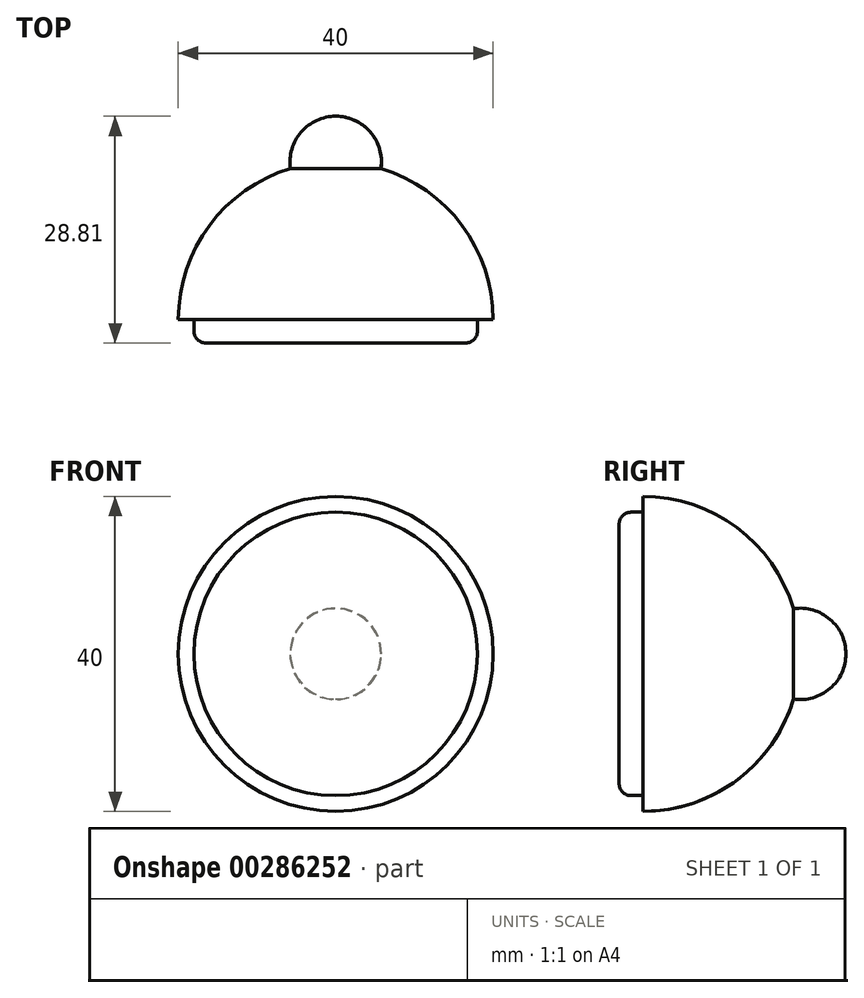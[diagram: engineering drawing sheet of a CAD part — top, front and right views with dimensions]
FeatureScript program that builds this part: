
annotation { "Feature Type Name" : "Feature", "Feature Type Description" : "" }
export const myFeature = defineFeature(function(context is Context, id is Id, definition is map)
    precondition{}
    {
        {
            var Q0;
            Q0=qCreatedBy(makeId("Top.planeOp"),FACE);
            var sketch = newSketch(context, id + "F0", { "sketchPlane" : qUnion([Q0])});
            skPoint(sketch, "E0", {"position": v(0, 20) * mm});
            skPoint(sketch, "E1", {"position": v(20, 0) * mm});
            skArc(sketch, "E2", {"start": v(20, 0) * mm, "mid": v(16.05, 11.94) * mm, "end": v(5.75, 19.16) * mm});
            skLineSegment(sketch, "E3", {"start": v(0, 14.2) * mm, "end": v(0, 0) * mm});
            skLineSegment(sketch, "E4", {"start": v(20, 0) * mm, "end": v(0, 0) * mm});
            skArc(sketch, "E5", {"start": v(5.75, 19.16) * mm, "mid": v(4.4, 23.8) * mm, "end": v(0, 25.8) * mm});
            skLineSegment(sketch, "E6", {"start": v(0, 14.2) * mm, "end": v(0, 25.8) * mm});
            skSolve(sketch);
        }
        {
            var Q0;
            Q0=makeQuery(id+"F0.imprint","IMPRINT",FACE,{"disambiguationData":[TD([[makeQuery(id+"F0.imprint","IMPRINT",EDGE,{"derivedFrom":sQuery(id+"F0.wireOp",EDGE,"E2")}),1.0]])]});
            var Q1;
            Q1=sQuery(id+"F0.wireOp",EDGE,"E6");
            revolve(context, id + "F1", {"entities" : qUnion([Q0]), "axis" : qUnion([Q1]), "revolveType" : RevolveType.FULL});
        }
        {
            var Q0;
            Q0=qCreatedBy(makeId("Front.planeOp"),FACE);
            var sketch = newSketch(context, id + "F2", { "sketchPlane" : qUnion([Q0])});
            skCircle(sketch, "E7", {"center": v(0, 0) * mm, "radius": 18 * mm});
            skSolve(sketch);
        }
        {
            var Q0;
            Q0 = qSketchRegion(id + "F2", true);
            extrude(context, id + "F3", {"entities" : qUnion([Q0]), "operationType" : NewBodyOperationType.ADD, "depth" : 3 * mm});
        }
        {
            var Q0;
            Q0=makeQuery(id+"F3.opExtrude","CAP_EDGE",EDGE,{"disambiguationData":[OSD([sQuery(id+"F2.wireOp",EDGE,"E7")])],"isStart":false});
            fillet(context, id + "F4", {"entities" : qUnion([Q0]), "radius" : 1.5 * mm, "tangentPropagation" : true, "allowEdgeOverflow" : false});
        }
    });
